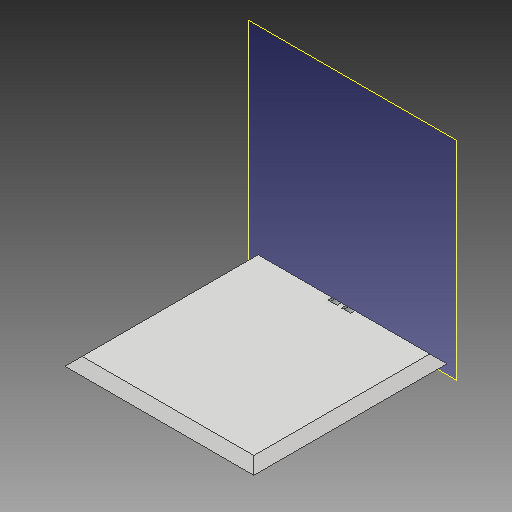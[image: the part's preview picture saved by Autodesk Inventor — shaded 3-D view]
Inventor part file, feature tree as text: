
AUTODESK INVENTOR PART (.ipt)
format: ipt  version: 2018 (Build 220112000, 112)  size: 135,168 bytes
history: native  units: mm
features: other x7, sketch x3, extrude x2, plane x1
ambient origin geometry x8: Origin, YZ Plane, XZ Plane, XY Plane, X Axis, Y Axis, Z Axis, Center Point
bodies: Volumenkörper1 (feature_tree)
feature tree (13):
  other  "Wand1.ipt"
  plane  "Arbeitsebene5"
  extrude  "Extrusion5"  Depth=10.0mm
  extrude  "Extrusion6"  Depth=21.0mm
  other  "Volumenkörper1::Wand1.ipt"
  other  "Bezeichnung1"
  sketch  "Skizze1"  dims[d0=10.0mm d33=5.0mm]
  other  "Arbeitspunkt6"
  sketch  "Skizze8"  dims[d34=5.0mm d35=21.0mm]
  sketch  "Skizze9"  dims[d36=174.5mm d37=30.0mm d38=0.0mm d39=5.0mm d40=5.0mm d41=21.0mm d42=30.0mm d43=0.0mm]
  parser-record x1  (decoder bookkeeping rows leaked as tree rows — omitted from the tree; the rows remain in map.json)
  other  "SmartCube_Quadratisch.iam"
  other  "Wand2_MIR:1"
note: 1 file-system path scrubbed to <path> (originals preserved in map.json)
